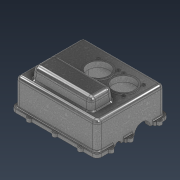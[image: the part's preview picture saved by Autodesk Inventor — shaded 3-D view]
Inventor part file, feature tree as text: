
AUTODESK INVENTOR PART (.ipt)
format: ipt  version: 2022 (Build 260153000, 153)  size: 834,048 bytes
history: native  units: mm
features: extrude x15, sketch x15, fillet x9, hole x2, chamfer x2, plane x1, mirror x1, projected_geometry x1
ambient origin geometry x8: Origin, YZ Plane, XZ Plane, XY Plane, X Axis, Y Axis, Z Axis, Center Point
bodies: Solid1 (feature_tree)
feature tree (46):
  extrude  "Extrusion1"  Depth=350.0mm
  extrude  "Extrusion2"  Depth=20.0mm TaperAngle=0.0deg
  extrude  "Extrusion3"  Depth=10.0mm TaperAngle=0.0deg
  extrude  "Extrusion5"  Depth=68.0mm
  extrude  "Extrusion6"  Depth=23.0mm
  extrude  "Extrusion7"  Depth=150.0mm TaperAngle=0.0deg
  extrude  "Extrusion8"  Depth=108.77mm
  sketch  "Sketch7"  dims[d33=50.0mm d34=150.0mm d35=0.0mm]
  extrude  "Extrusion9"  TaperAngle=0.0deg  [1 undecoded]
  extrude  "Extrusion10"  Depth=4.0mm TaperAngle=0.0deg
  hole  "Hole5"  [1 undecoded]
  extrude  "Extrusion11"  Depth=15.0mm
  extrude  "Extrusion12"  Depth=20.0mm TaperAngle=0.0deg
  extrude  "Extrusion13"  Depth=25.0mm
  extrude  "Extrusion14"  TaperAngle=0.0deg  [1 undecoded]
  extrude  "Extrusion15"  Depth=10.0mm
  fillet  "Fillet1"  Radius=40.0mm
  fillet  "Fillet2"  Radius=21.76mm
  chamfer  "Chamfer1"  Distance=228.068mm
  fillet  "Fillet3"  Radius=10.0mm
  fillet  "Fillet4"  Radius=10.0mm
  fillet  "Fillet5"  Radius=75.0mm
  fillet  "Fillet8"  Radius=100.0mm
  chamfer  "Chamfer2"  Distance=260.0mm
  plane  "Work Plane1"
  mirror  "Mirror1"
  extrude  "Extrusion16"  Depth=10.0mm
  fillet  "Fillet6"  Radius=5.0mm
  fillet  "Fillet7"  Radius=5.0mm
  fillet  "Fillet9"  Radius=30.0mm
  hole  "Hole6"  [1 undecoded]
  sketch  "Sketch2"  dims[d0=290.0mm d1=350.0mm]
  sketch  "Sketch3"  dims[d19=10.0mm d20=20.0mm d21=0.0mm]
  sketch  "Sketch4"  dims[d22=100.0mm d23=0.0mm d24=10.0mm d25=0.0mm]
  sketch  "Sketch5"  dims[d28=23.172mm d29=68.0mm]
  sketch  "Sketch6"  dims[d30=150.0mm d31=0.0mm d32=23.0mm]
  sketch  "Sketch8"  dims[d36=160.67mm d37=108.77mm]
  sketch  "Sketch10"  dims[d38=90.0mm d39=0.0mm d40=0.0mm]
  sketch  "Sketch11"  dims[d41=105.0mm d42=4.0mm d43=20.0mm d44=0.0mm d45=0.0mm]
  sketch  "Sketch12"  dims[d46=121.5mm d47=121.5mm]
  projected_geometry  "Projected Loop1"
  sketch  "Sketch13"  dims[d48=85.5mm d49=15.0mm]
  sketch  "Sketch14"  dims[d50=20.0mm d51=0.0mm d59=2.0mm d60=0.0mm]
  sketch  "Sketch15"  dims[d82=8.376mm d83=17.0mm d84=4.0mm d85=2.0mm d86=90.0deg d87=17.0mm d88=20.594885mm d89=25.0mm]
  sketch  "Sketch16"  dims[d90=70.0mm d91=0.0mm d92=0.0mm]
  sketch  "Sketch17"  dims[d93=132.118mm d94=30.0mm d95=40.0mm d96=21.76mm d97=228.068mm d98=10.0mm d99=0.0mm d100=10.0mm d101=0.0mm d105=75.0mm d106=100.0mm d107=260.0mm d108=50.0mm d109=-0.872665mm d110=5.0mm d111=5.0mm d112=30.0mm d113=30.0mm d114=50.0mm d115=-0.872665mm d116=15.0mm d117=20.0mm d118=5.0mm d119=2.0mm d120=45.0deg d121=10.0mm d122=5.0mm d123=20.0mm d124=5.0mm d125=2.0mm d126=45.0deg d127=50.0mm d128=10.0mm d129=10.0mm d130=10.0mm d131=10.0mm d132=20.0mm d133=28.75mm d134=28.75mm d135=30.0mm d136=30.0mm d137=90.0mm d138=70.0mm d139=110.0mm d140=110.0mm d141=50.0mm d142=90.0mm d143=90.0mm d144=90.0mm d145=15.0mm d146=0.0mm d147=10.0mm d148=10.0mm d149=10.0mm d150=10.0mm d151=10.0mm d152=10.0mm d153=20.0mm d154=5.0mm d155=11.0mm d156=5.0mm d157=8.0mm d158=10.0mm d159=4.0mm d160=2.0mm d161=90.0deg d162=10.0mm d163=20.594885mm d68=1.0mm d69=1.0mm d70=1.0mm d71=0.15mm d72=0.25mm d73=0.375mm d74=14.3117mm d75=24.0mm d76=20.594885mm d77=0.0625mm d78=0.75mm d79=0.375mm]
note: 4 required parameter values undecoded (feature->parameter linkage not recoverable at this tier; creation-order binding heuristic only, values carry confidence <= 0.55)
